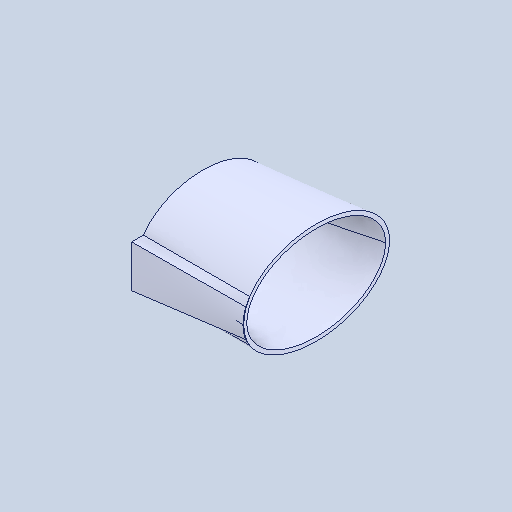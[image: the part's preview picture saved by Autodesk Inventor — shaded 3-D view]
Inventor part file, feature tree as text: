
AUTODESK INVENTOR PART (.ipt)
format: ipt  version: 2022 (Build 260153000, 153)  size: 223,744 bytes
history: mixed  units: mm
features: other x2, shell x1, loft x1, imported_body x1
ambient origin geometry x8: Origin, YZ Plane, XZ Plane, XY Plane, X Axis, Y Axis, Z Axis, Center Point
bodies: Body1 (imported_parasolid), Body2 (imported_parasolid)
feature tree (5):
  other  "Sólido1"
  other  "Sólido2"
  shell  "Shell1"  [1 undecoded]
  loft  "Loft28"
  imported_body  NMx_Import_Brep_tag  [imported B-rep: ~7 faces, bbox_mm=None]
note: 1 required parameter value undecoded (feature->parameter linkage not recoverable at this tier; creation-order binding heuristic only, values carry confidence <= 0.55)
